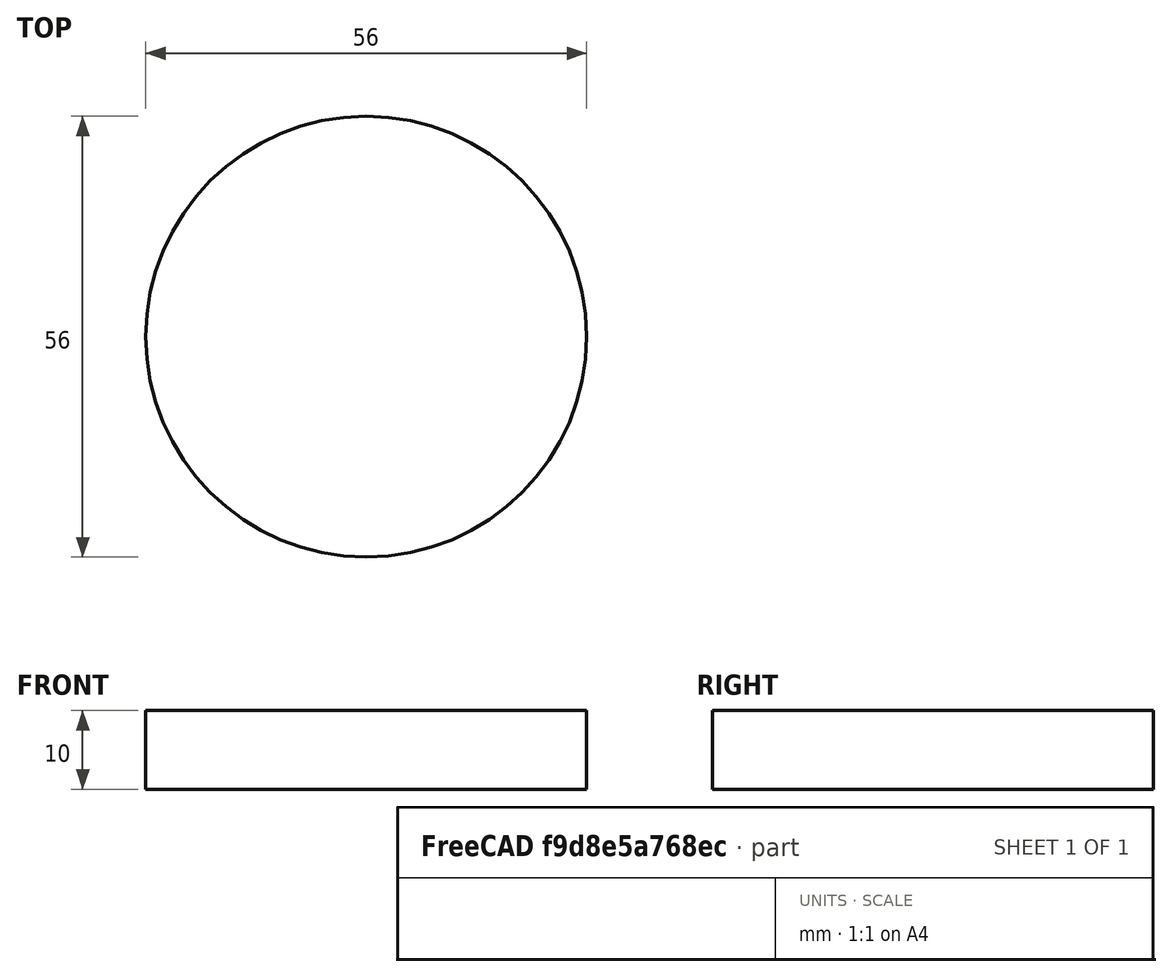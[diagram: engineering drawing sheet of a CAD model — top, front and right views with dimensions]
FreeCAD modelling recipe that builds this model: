
FCSTD DOCUMENT  (FreeCAD 0.19R24291 (Git))
Label: Hub_Flange_Cover_Front
License: All rights reserved
LicenseURL: http://en.wikipedia.org/wiki/All_rights_reserved
objects: Sketcher::SketchObject×1, PartDesign::Pad×1, PartDesign::Body×1, Spreadsheet::Sheet×1
note: 4 computed .brp shape members not serialized (recipe doc carries the construction recipe); baked Part::Feature solids carry a one-line shape summary decoded from their .brp
EXTERNAL_REF file=../../Master_of_Puppets.FCStd obj=Hub

FEATURE [Sketcher::SketchObject] Sketch
  FullyConstrained = true
  MapMode = 5
  Support = -> [XY_Plane001]
  expr: Constraints[1] = Spreadsheet.RotorSidePadRadius
  sketch-geometry (1):
    g0: Circle CenterX=0 CenterY=0 CenterZ=0 NormalX=0 NormalY=0 NormalZ=1 AngleXU=0 Radius=28
  constraints (2):
    c: Coincident(g0,g-1)
    c: Radius(g0) = 28
FEATURE [PartDesign::Pad] Pad
  AllowMultiFace = false
  Direction = (1,1,1)
  Length = 10
  Length2 = 100
  Profile = -> Sketch
  Type = 0
  expr: Length = Spreadsheet.CoverThickness
FEATURE [PartDesign::Body] PadBody  label="Hub_Flange_Cover_Front"
  Group = -> [Sketch,Pad]
  Origin = -> Origin001
  Placement = pos=(0,0,-40) rot=(0,0,1;0rad)
  Tip = -> Pad
  expr: .Placement.Base.z = -40
FEATURE [Spreadsheet::Sheet] Spreadsheet
  cells = A1=Inputs; A2=CoverThickness; B2(CoverThickness)==Master_of_Puppets#Hub.CoverThickness; A3=RotorSidePadRadius; B3(RotorSidePadRadius)==Master_of_Puppets#Hub.RotorSidePadRadius
